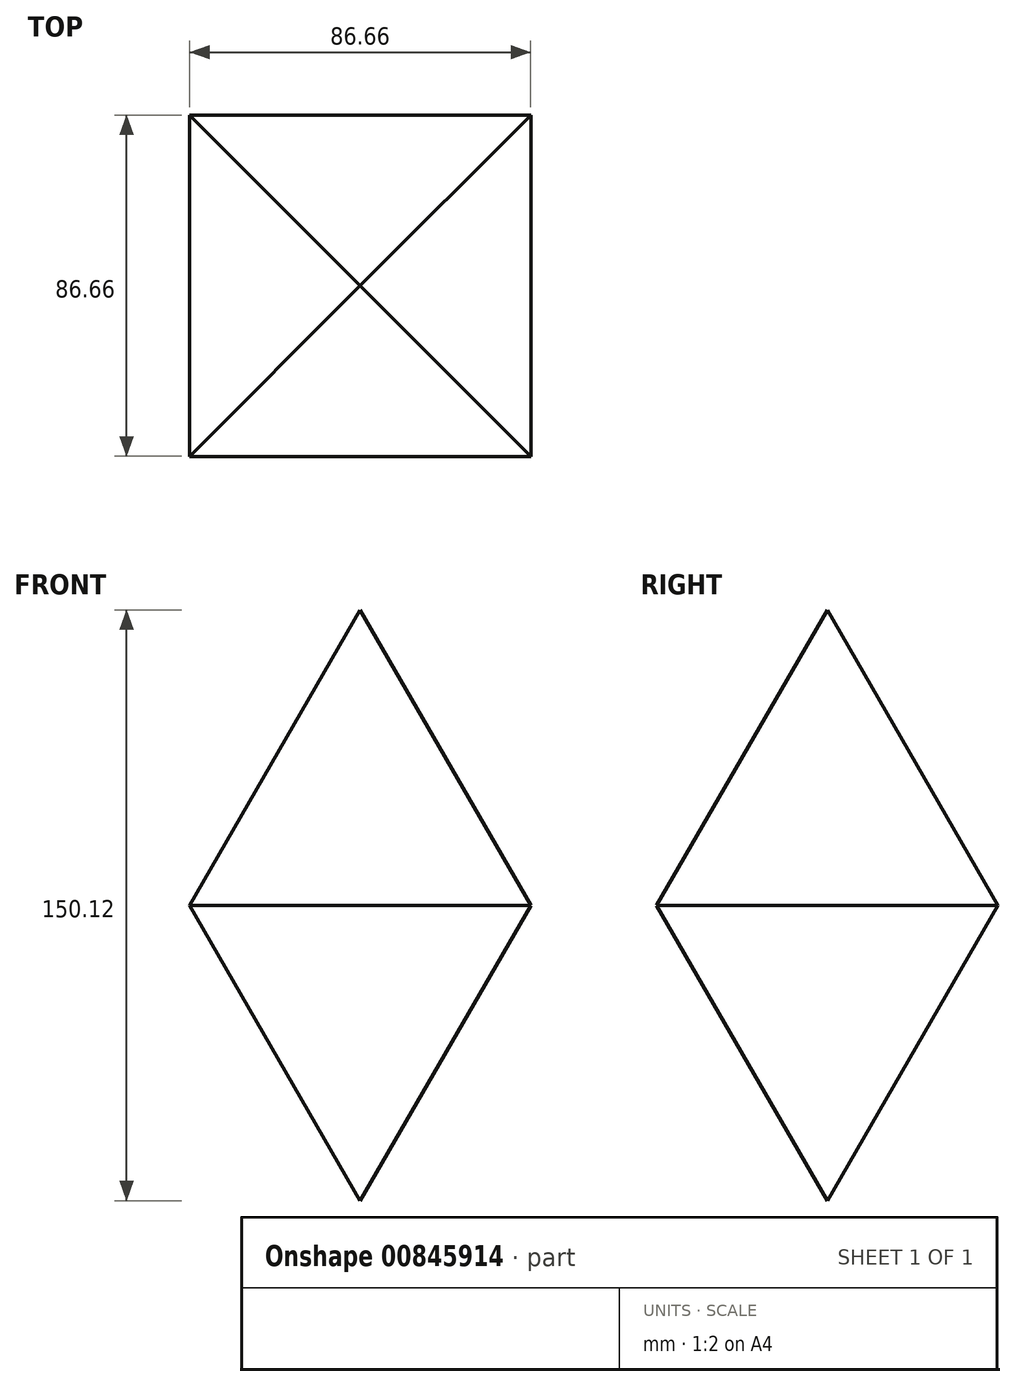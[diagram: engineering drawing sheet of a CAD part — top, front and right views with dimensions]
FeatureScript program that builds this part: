
annotation { "Feature Type Name" : "Feature", "Feature Type Description" : "" }
export const myFeature = defineFeature(function(context is Context, id is Id, definition is map)
    precondition{}
    {
        {
            var Q0;
            Q0=qCreatedBy(makeId("Top.planeOp"),FACE);
            var sketch = newSketch(context, id + "F0", { "sketchPlane" : qUnion([Q0])});
            skLineSegment(sketch, "E0.bottom", {"start": v(43.33, 43.33) * mm, "end": v(-43.33, 43.33) * mm});
            skLineSegment(sketch, "E0.top", {"start": v(43.33, -43.33) * mm, "end": v(-43.33, -43.33) * mm});
            skLineSegment(sketch, "E0.left", {"start": v(43.33, 43.33) * mm, "end": v(43.33, -43.33) * mm});
            skLineSegment(sketch, "E0.right", {"start": v(-43.33, 43.33) * mm, "end": v(-43.33, -43.33) * mm});
            skPoint(sketch, "E0.middle", {"position": v(0, 0) * mm});
            skSolve(sketch);
        }
        {
            var Q0;
            Q0 = qSketchRegion(id + "F0", true);
            extrude(context, id + "F1", {"entities" : qUnion([Q0]), "depth" : 84.84 * mm, "offsetDistance" : 25.4 * mm, "hasDraft" : true, "draftAngle" : 30 * degree, "draftPullDirection" : true, "hasSecondDirection" : true, "secondDirectionOppositeDirection" : true, "secondDirectionDepth" : 118.36 * mm, "hasSecondDirectionDraft" : true, "secondDirectionDraftAngle" : 30 * degree, "secondDirectionDraftPullDirection" : true});
        }
    });
